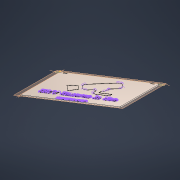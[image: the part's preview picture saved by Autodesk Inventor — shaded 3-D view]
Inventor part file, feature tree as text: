
AUTODESK INVENTOR PART (.ipt)
format: ipt  version: 2021 (Build 250183000, 183)  size: 6,029,824 bytes
history: native  units: mm
features: other x5, extrude x4, sketch x3, fillet x2
ambient origin geometry x8: Origin, YZ Plane, XZ Plane, XY Plane, X Axis, Y Axis, Z Axis, Center Point
bodies: Solid1 (feature_tree), Solid2 (feature_tree)
feature tree (14):
  other  "Blocks"
  sketch  "Sketch1"  dims[d2=250.0mm d3=190.0mm]
  extrude  "Extrusion1"  Depth=190.0mm
  extrude  "Extrusion2"  Depth=0.6mm TaperAngle=0.0deg
  extrude  "Extrusion3"  Depth=10.0mm
  extrude  "Extrusion4"  Depth=5.0mm
  fillet  "Fillet1"  Radius=3.0mm
  fillet  "Fillet2"  Radius=10.0mm
  other  "cctv"
  other  "pls"
  sketch  "Sketch2"  dims[d4=3.0mm d5=0.0mm d6=0.6mm d7=0.0mm]
  sketch  "Sketch3"  dims[d8=0.6mm d9=0.0mm d10=10.0mm d11=3.0mm d12=3.0mm d13=10.0mm d14=20.0mm d16=220.0mm d17=10.0mm d19=10.0mm d21=0.0mm d22=0.0mm d23=1.5mm d24=5.0mm]
  other  "cctv:1"
  other  "pls:1"
